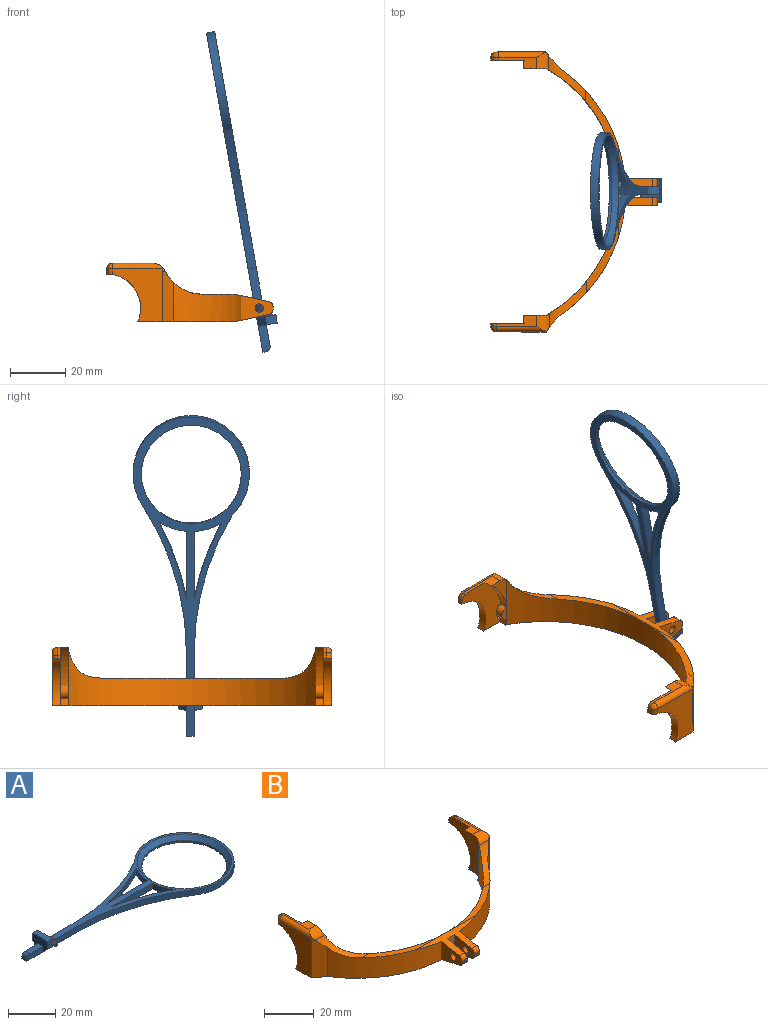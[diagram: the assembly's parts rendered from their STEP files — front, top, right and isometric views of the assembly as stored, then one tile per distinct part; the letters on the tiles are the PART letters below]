
ASSEMBLY  parts=2 mates=1
PART A: 35 faces, bbox 117x42x7 mm
  f0: plane 18.01x7mm, normal (0,-1,0), area 55.8mm2, adj f8,f17,f18,f21,f27,f32
  f1: plane 18.01x7mm, normal (0,1,0), area 55.8mm2, adj f2,f4,f17,f18,f23,f32
  f2: plane 7x3mm, normal (1,0,0), area 16.5mm2, adj f1,f28,f31,f33
  f3: plane 7.52x2.8mm, normal (0,0,1), area 21.1mm2, adj f5,f7,f20,f29
  f4: cylinder r=100mm len=50.59mm, axis (0,0,-1), area 159.1mm2, adj f1,f13,f17,f18
  f5: plane 9.52x3mm, normal (0,1,0), area 27.7mm2, adj f3,f6,f18,f20,f29
  f6: plane 2.8x1mm, normal (-1,0,0), area 2.8mm2, adj f5,f7,f18,f20
  f7: plane 9.52x3mm, normal (0,-1,0), area 27.7mm2, adj f3,f6,f18,f20,f29
  f8: cylinder r=100mm len=54.13mm, axis (0,0,-1), area 171.6mm2, adj f0,f13,f17,f18
  f9: plane 24.42x3mm, normal (0,1,0), area 73.3mm2, adj f10,f14,f17,f18
  f10: cylinder r=102mm len=27.37mm, axis (0,0,-1), area 87.4mm2, adj f9,f14,f17,f18
  f11: plane 24.46x3mm, normal (0,-1,0), area 73.4mm2, adj f12,f15,f17,f18
  f12: cylinder r=21mm len=10.07mm, axis (0,0,-1), area 32.4mm2, adj f11,f15,f17,f18
  f13: cylinder r=21mm len=42mm, axis (0,0,-1), area 283.7mm2, adj f4,f8,f17,f18
  f14: cylinder r=21mm len=9.72mm, axis (0,0,-1), area 30.8mm2, adj f9,f10,f17,f18
  f15: cylinder r=102mm len=28.03mm, axis (0,0,-1), area 89.7mm2, adj f11,f12,f17,f18
  f16: cylinder r=18mm len=36mm, axis (0,0,-1), area 113.1mm2, adj f18,f19
  f17: plane 99.61x42mm, normal (0,0,1), area 442.8mm2, adj f0,f1,f4,f8,f9,f10,f11,f12
  f18: plane 117.02x42mm, normal (0,0,-1), area 730.3mm2, adj f0,f1,f4,f5,f6,f7,f8,f9
  f19: cone r=18mm half-angle=45deg, axis (0,0,1), area 337.7mm2, adj f16,f17
  f20: cylinder r=2mm len=2.8mm, axis (0,1,0), area 8.8mm2, adj f3,f5,f6,f7
  f21: cylinder r=1mm len=2mm, axis (0,1,0), area 8.2mm2, adj f0,f25
  f22: plane 1x1mm, normal (0,-1,0), area 0.8mm2, adj f25
  f23: cylinder r=1mm len=2mm, axis (0,-1,0), area 8.2mm2, adj f1,f26
  f24: plane 1x1mm, normal (0,1,0), area 0.8mm2, adj f26
  f25: cone r=0.5mm half-angle=45deg, axis (0,1,0), area 3.3mm2, adj f21,f22
  f26: cone r=1mm half-angle=45deg, axis (0,-1,0), area 3.3mm2, adj f23,f24
  f27: plane 7x3mm, normal (1,0,0), area 16.5mm2, adj f0,f30,f31,f34
  f28: plane 4x3mm, normal (0,1,0), area 12mm2, adj f2,f29,f31,f33
  f29: plane 8.8x7mm, normal (-1,0,0), area 44.2mm2, adj f3,f5,f7,f28,f30,f31,f33,f34
  f30: plane 4x3mm, normal (0,-1,0), area 12mm2, adj f27,f29,f31,f34
  f31: plane 8.8x3mm, normal (0,0,1), area 26.4mm2, adj f2,f27,f28,f29,f30,f32
  f32: cylinder r=5mm len=4.9mm, axis (0,-1,0), area 19.2mm2, adj f0,f1,f17,f31
  f33: plane 3x3mm, normal (0,0.71,-0.71), area 12.7mm2, adj f2,f18,f28,f29
  f34: plane 3x3mm, normal (0,-0.71,-0.71), area 12.7mm2, adj f18,f27,f29,f30
PART B: 60 faces, bbox 101.8x60.2x23.3 mm
  f0: plane 36.23x11.55mm, normal (0,0,1), area 69.5mm2, adj f2,f8,f18,f53
  f1: plane 50.38x34.85mm, normal (0,0,-1), area 154.1mm2, adj f4,f8,f10,f11,f34,f38,f39,f40
  f2: cylinder r=53.68mm len=40.19mm, axis (0,0,-1), area 510.8mm2, adj f0,f7,f18,f29,f50,f52,f53
  f3: cylinder r=53.68mm len=8.89mm, axis (0,0,-1), area 35.6mm2, adj f47,f49,f52,f53
  f4: cylinder r=20mm len=3mm, axis (-1,0,0), area 7.7mm2, adj f1,f11,f16,f40
  f5: plane 36.4x11.71mm, normal (0,0,1), area 70.1mm2, adj f8,f10,f20,f53
  f6: cylinder r=20mm len=13.62mm, axis (-1,0,0), area 48.7mm2, adj f9,f14,f15,f22
  f7: plane 50.38x34.86mm, normal (0,0,-1), area 152.8mm2, adj f2,f8,f9,f12,f22,f23,f27,f28
  f8: cylinder r=51.04mm len=89mm, axis (0,0,-1), area 1179.2mm2, adj f0,f1,f5,f7,f9,f11,f18,f19
  f9: plane 21.12x8.16mm, normal (1,0,0), area 48.6mm2, adj f6,f7,f8,f12,f14,f15,f19
  f10: cylinder r=53.68mm len=39.2mm, axis (0,0,-1), area 480.3mm2, adj f1,f5,f20,f41,f46,f52,f53
  f11: plane 21.12x8.16mm, normal (-1,0,0), area 48.4mm2, adj f1,f4,f8,f13,f16,f17,f21
  f12: cylinder r=20mm len=3mm, axis (-1,0,0), area 7.7mm2, adj f7,f9,f14,f22
  f13: cylinder r=20mm len=13.62mm, axis (-1,0,0), area 48.7mm2, adj f11,f16,f17,f40
  f14: cylinder r=2.5mm len=4.99mm, axis (-1,0,0), area 22.6mm2, adj f6,f9,f12,f22
  f15: plane 14.57x4mm, normal (0,0,1), area 28.8mm2, adj f6,f9,f19,f22,f25,f31
  f16: cylinder r=2.5mm len=4.99mm, axis (1,0,0), area 22.6mm2, adj f4,f11,f13,f40
  f17: plane 13.41x4mm, normal (0,0,1), area 27.1mm2, adj f11,f13,f21,f36,f40,f43
  f18: cylinder r=15mm len=16.72mm, axis (1,0,0), area 61.9mm2, adj f0,f2,f8,f19,f29,f30
  f19: cylinder r=5mm len=6.53mm, axis (1,0,0), area 28.6mm2, adj f8,f9,f15,f18,f30,f31
  f20: cylinder r=15mm len=16.7mm, axis (-1,0,0), area 64.4mm2, adj f5,f8,f10,f21,f41,f42
  f21: cylinder r=5mm len=6.47mm, axis (-1,0,0), area 28.6mm2, adj f8,f11,f17,f20,f42,f43
  f22: plane 21.12x19.84mm, normal (1,0,0), area 194mm2, adj f6,f7,f12,f14,f15,f25,f26,f27
  f23: plane 18.12x0.05mm, normal (0,-1,0), area 0.9mm2, adj f7,f24,f28,f29
  f24: cylinder r=3mm len=0.36mm, axis (1,0,0), area 0mm2, adj f23,f28,f30
  f25: cylinder r=2mm len=2mm, axis (1,0,0), area 3.1mm2, adj f15,f22,f26,f32
  f26: plane 1.87x1mm, normal (0,1,0), area 1.9mm2, adj f22,f25,f27,f33
  f27: cylinder r=12.25mm len=17.25mm, axis (1,0,0), area 72.3mm2, adj f7,f22,f26,f28,f33
  f28: plane 19.13x18.04mm, normal (-1,0,0), area 201.1mm2, adj f7,f23,f24,f27,f30,f31,f33
  f29: plane 18.12x5.26mm, normal (-0.6,-0.8,0), area 109.5mm2, adj f2,f7,f18,f23,f30
  f30: bspline ~5.6x4.84mm, area 1.8mm2, adj f18,f19,f24,f28,f29,f31
  f31: cylinder r=2mm len=18.1mm, axis (0,-1,0), area 52.3mm2, adj f15,f19,f28,f30,f32
  f32: sphere r=2mm, area 4mm2, adj f25,f31,f33
  f33: cylinder r=2mm len=2.03mm, axis (0,0,1), area 6.1mm2, adj f26,f27,f28,f32
  f34: cylinder r=12.26mm len=17.26mm, axis (-1,0,0), area 72.4mm2, adj f1,f35,f39,f40,f45
  f35: plane 1x0.86mm, normal (0,1,0), area 0.9mm2, adj f34,f36,f40,f45
  f36: cylinder r=3mm len=3mm, axis (-1,0,0), area 4.7mm2, adj f17,f35,f40,f44
  f37: cylinder r=3mm len=0.77mm, axis (-1,0,0), area 0.1mm2, adj f38,f39,f42
  f38: plane 18.12x0.29mm, normal (0,-1,0), area 5.2mm2, adj f1,f37,f39,f41
  f39: plane 19.12x18mm, normal (1,0,0), area 200.7mm2, adj f1,f34,f37,f38,f42,f43,f44,f45
  f40: plane 21.12x19.84mm, normal (-1,0,0), area 192.7mm2, adj f1,f4,f13,f16,f17,f34,f35,f36
  f41: plane 18.12x6.01mm, normal (0.67,-0.74,0), area 127.1mm2, adj f1,f10,f20,f38,f42
  f42: bspline ~6.64x5.67mm, area 1.4mm2, adj f20,f21,f37,f39,f41,f43
  f43: cylinder r=2mm len=17.08mm, axis (0,-1,0), area 48.6mm2, adj f17,f21,f39,f42,f44
  f44: torus R=1mm, axis (1,0,0), area 11.2mm2, adj f36,f39,f43,f45
  f45: cylinder r=2mm len=2mm, axis (0,0,-1), area 3mm2, adj f34,f35,f39,f44
  f46: plane 11.6x8.97mm, normal (1,0,0), area 67.1mm2, adj f10,f48,f52,f53,f56,f57,f59
  f47: plane 11.4x8.89mm, normal (-1,0,0), area 65.4mm2, adj f3,f48,f52,f53,f56,f57,f59
  f48: plane 3x0.77mm, normal (0,-1,0), area 2.3mm2, adj f46,f47,f56,f57
  f49: plane 11.4x8.89mm, normal (1,0,0), area 65.4mm2, adj f3,f51,f52,f53,f54,f55,f58
  f50: plane 11.6x8.97mm, normal (-1,0,0), area 67.1mm2, adj f2,f51,f52,f53,f54,f55,f58
  f51: plane 3x0.77mm, normal (0,-1,0), area 2.3mm2, adj f49,f50,f54,f55
  f52: plane 33.37x12.56mm, normal (0,-0.21,-0.98), area 120.8mm2, adj f1,f2,f3,f7,f8,f10,f46,f47
  f53: plane 33.37x12.56mm, normal (0,-0.21,0.98), area 120.8mm2, adj f0,f2,f3,f5,f8,f10,f46,f47
  f54: cylinder r=2mm len=3mm, axis (1,0,0), area 8.2mm2, adj f49,f50,f51,f52
  f55: cylinder r=2mm len=3mm, axis (1,0,0), area 8.2mm2, adj f49,f50,f51,f53
  f56: cylinder r=2mm len=3mm, axis (1,0,0), area 8.2mm2, adj f46,f47,f48,f52
  f57: cylinder r=2mm len=3mm, axis (1,0,0), area 8.2mm2, adj f46,f47,f48,f53
  f58: cylinder r=1.5mm len=3mm, axis (1,0,0), area 28.3mm2, adj f49,f50
  f59: cylinder r=1.5mm len=3mm, axis (1,0,0), area 28.3mm2, adj f46,f47
PLACE A rot(axis=(0.64,0,0.77),180deg) t=(-14.7,22.79,-74.76)mm
PLACE B rot(axis=(0,0,1),90deg) t=(-71.04,22.19,-63.74)mm
MATE cylindrical A.f25 <-> B.f58  axis (0,1,0) through (-16,24.19,-58.74)mm
